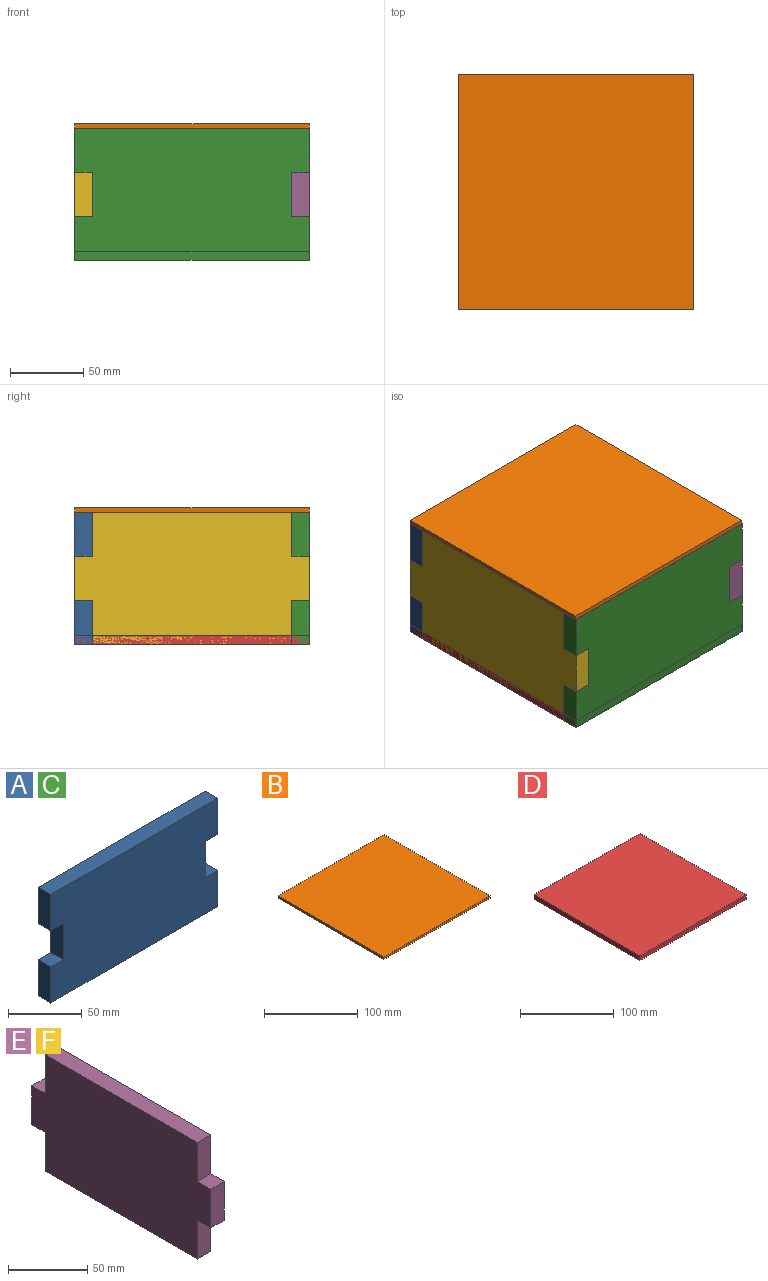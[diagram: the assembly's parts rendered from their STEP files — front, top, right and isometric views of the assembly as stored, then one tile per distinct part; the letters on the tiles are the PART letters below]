
ASSEMBLY  parts=6 mates=5
PART A: 14 faces, bbox 160x12x90 mm
  f0: plane 12x12mm, normal (0,0,1), area 144mm2, adj f1,f11,f12,f13
  f1: plane 30x12mm, normal (1,0,0), area 360mm2, adj f0,f2,f12,f13
  f2: plane 12x12mm, normal (0,0,-1), area 144mm2, adj f1,f3,f12,f13
  f3: plane 30x12mm, normal (1,0,0), area 360mm2, adj f2,f4,f12,f13
  f4: plane 160x12mm, normal (0,0,1), area 1920mm2, adj f3,f5,f12,f13
  f5: plane 30x12mm, normal (-1,0,0), area 360mm2, adj f4,f6,f12,f13
  f6: plane 12x12mm, normal (0,0,-1), area 144mm2, adj f5,f7,f12,f13
  f7: plane 30x12mm, normal (-1,0,0), area 360mm2, adj f6,f8,f12,f13
  f8: plane 12x12mm, normal (0,0,1), area 144mm2, adj f7,f9,f12,f13
  f9: plane 30x12mm, normal (-1,0,0), area 360mm2, adj f8,f10,f12,f13
  f10: plane 160x12mm, normal (0,0,-1), area 1920mm2, adj f9,f11,f12,f13
  f11: plane 30x12mm, normal (1,0,0), area 360mm2, adj f0,f10,f12,f13
  f12: plane 160x90mm, normal (0,-1,0), area 13680mm2, adj f0,f1,f2,f3,f4,f5,f6,f7
  f13: plane 160x90mm, normal (0,1,0), area 13680mm2, adj f0,f1,f2,f3,f4,f5,f6,f7
PART B: 6 faces, bbox 160x160x3 mm
  f0: plane 160x3mm, normal (1,0,0), area 480mm2, adj f1,f3,f4,f5
  f1: plane 160x3mm, normal (0,1,0), area 480mm2, adj f0,f2,f4,f5
  f2: plane 160x3mm, normal (-1,0,0), area 480mm2, adj f1,f3,f4,f5
  f3: plane 160x3mm, normal (0,-1,0), area 480mm2, adj f0,f2,f4,f5
  f4: plane 160x160mm, normal (0,0,1), area 25600mm2, adj f0,f1,f2,f3
  f5: plane 160x160mm, normal (0,0,-1), area 25600mm2, adj f0,f1,f2,f3
PART C: same geometry as A
PART D: 6 faces, bbox 160x160x6 mm
  f0: plane 160x6mm, normal (1,0,0), area 960mm2, adj f1,f3,f4,f5
  f1: plane 160x6mm, normal (0,1,0), area 960mm2, adj f0,f2,f4,f5
  f2: plane 160x6mm, normal (-1,0,0), area 960mm2, adj f1,f3,f4,f5
  f3: plane 160x6mm, normal (0,-1,0), area 960mm2, adj f0,f2,f4,f5
  f4: plane 160x160mm, normal (0,0,1), area 25600mm2, adj f0,f1,f2,f3
  f5: plane 160x160mm, normal (0,0,-1), area 25600mm2, adj f0,f1,f2,f3
PART E: 14 faces, bbox 12x160x90 mm
  f0: plane 12x12mm, normal (0,0,-1), area 144mm2, adj f1,f11,f12,f13
  f1: plane 30x12mm, normal (0,1,0), area 360mm2, adj f0,f2,f12,f13
  f2: plane 12x12mm, normal (0,0,1), area 144mm2, adj f1,f3,f12,f13
  f3: plane 30x12mm, normal (0,1,0), area 360mm2, adj f2,f4,f12,f13
  f4: plane 136x12mm, normal (0,0,1), area 1632mm2, adj f3,f5,f12,f13
  f5: plane 30x12mm, normal (0,-1,0), area 360mm2, adj f4,f6,f12,f13
  f6: plane 12x12mm, normal (0,0,1), area 144mm2, adj f5,f7,f12,f13
  f7: plane 30x12mm, normal (0,-1,0), area 360mm2, adj f6,f8,f12,f13
  f8: plane 12x12mm, normal (0,0,-1), area 144mm2, adj f7,f9,f12,f13
  f9: plane 30x12mm, normal (0,-1,0), area 360mm2, adj f8,f10,f12,f13
  f10: plane 136x12mm, normal (0,0,-1), area 1632mm2, adj f9,f11,f12,f13
  f11: plane 30x12mm, normal (0,1,0), area 360mm2, adj f0,f10,f12,f13
  f12: plane 160x90mm, normal (1,0,0), area 12960mm2, adj f0,f1,f2,f3,f4,f5,f6,f7
  f13: plane 160x90mm, normal (-1,0,0), area 12960mm2, adj f0,f1,f2,f3,f4,f5,f6,f7
PART F: same geometry as E
PLACE A t=(-135.86,160.53,12.44)mm
PLACE B t=(-135.86,160.53,102.44)mm
PLACE C t=(-135.86,12.53,12.44)mm
PLACE D t=(-135.86,160.53,12.44)mm
PLACE E t=(12.14,12.53,12.44)mm
PLACE F t=(-135.86,12.53,12.44)mm
MATE fastened B.f5 <-> C.f4  axis (0,0,-1) through (24.14,0.53,102.44)mm
MATE fastened F.f1 <-> A.f13  axis (0,1,0) through (-135.86,160.53,72.44)mm
MATE fastened F.f13 <-> C.f5  axis (-1,0,0) through (-135.86,0.53,72.44)mm
MATE fastened D.f5 <-> A.f10  axis (0,0,-1) through (-135.86,160.53,12.44)mm
MATE fastened E.f7 <-> C.f12  axis (0,-1,0) through (24.14,0.53,72.44)mm
